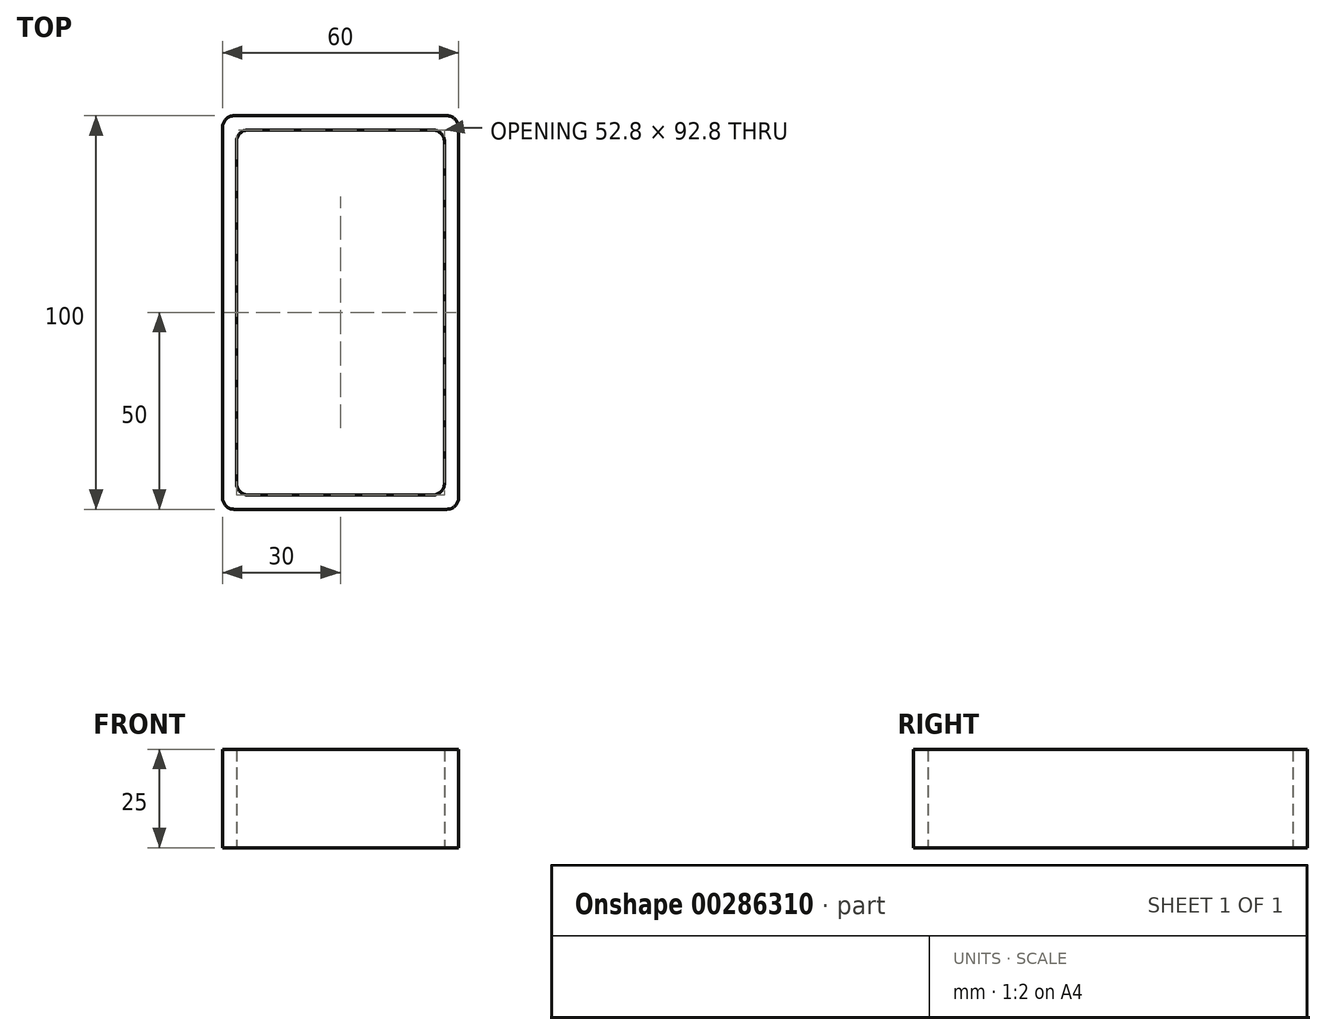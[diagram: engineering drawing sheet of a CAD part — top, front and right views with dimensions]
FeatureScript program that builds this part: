
annotation { "Feature Type Name" : "Feature", "Feature Type Description" : "" }
export const myFeature = defineFeature(function(context is Context, id is Id, definition is map)
    precondition{}
    {
        {
            var Q0;
            Q0=qCreatedBy(makeId("Top.planeOp"),FACE);
            var sketch = newSketch(context, id + "F0", { "sketchPlane" : qUnion([Q0])});
            skLineSegment(sketch, "E0", {"start": v(0, -3) * mm, "end": v(0, -97) * mm});
            skLineSegment(sketch, "E1", {"start": v(3, -100) * mm, "end": v(57, -100) * mm});
            skLineSegment(sketch, "E2", {"start": v(60, -97) * mm, "end": v(60, -3) * mm});
            skLineSegment(sketch, "E3", {"start": v(57, 0) * mm, "end": v(3, 0) * mm});
            skLineSegment(sketch, "E4", {"start": v(6.6, -3.6) * mm, "end": v(53.4, -3.6) * mm});
            skLineSegment(sketch, "E5", {"start": v(56.4, -6.6) * mm, "end": v(56.4, -93.4) * mm});
            skLineSegment(sketch, "E6", {"start": v(53.4, -96.4) * mm, "end": v(6.6, -96.4) * mm});
            skLineSegment(sketch, "E7", {"start": v(3.6, -93.4) * mm, "end": v(3.6, -6.6) * mm});
            skPoint(sketch, "E8.visualSharp", {"position": v(0, 0) * mm});
            skArc(sketch, "E8.filletArc", {"start": v(3, 0) * mm, "mid": v(0.88, -0.88) * mm, "end": v(0, -3) * mm});
            skPoint(sketch, "E9.visualSharp", {"position": v(3.6, -3.6) * mm});
            skArc(sketch, "E9.filletArc", {"start": v(6.6, -3.6) * mm, "mid": v(4.48, -4.48) * mm, "end": v(3.6, -6.6) * mm});
            skPoint(sketch, "E10.visualSharp", {"position": v(60, 0) * mm});
            skArc(sketch, "E10.filletArc", {"start": v(60, -3) * mm, "mid": v(59.12, -0.88) * mm, "end": v(57, 0) * mm});
            skPoint(sketch, "E11.visualSharp", {"position": v(56.4, -3.6) * mm});
            skArc(sketch, "E11.filletArc", {"start": v(56.4, -6.6) * mm, "mid": v(55.52, -4.48) * mm, "end": v(53.4, -3.6) * mm});
            skPoint(sketch, "E12.visualSharp", {"position": v(56.4, -96.4) * mm});
            skArc(sketch, "E12.filletArc", {"start": v(53.4, -96.4) * mm, "mid": v(55.52, -95.52) * mm, "end": v(56.4, -93.4) * mm});
            skPoint(sketch, "E13.visualSharp", {"position": v(60, -100) * mm});
            skArc(sketch, "E13.filletArc", {"start": v(57, -100) * mm, "mid": v(59.12, -99.12) * mm, "end": v(60, -97) * mm});
            skPoint(sketch, "E14.visualSharp", {"position": v(3.6, -96.4) * mm});
            skArc(sketch, "E14.filletArc", {"start": v(3.6, -93.4) * mm, "mid": v(4.48, -95.52) * mm, "end": v(6.6, -96.4) * mm});
            skPoint(sketch, "E15.visualSharp", {"position": v(0, -100) * mm});
            skArc(sketch, "E15.filletArc", {"start": v(0, -97) * mm, "mid": v(0.88, -99.12) * mm, "end": v(3, -100) * mm});
            skSolve(sketch);
        }
        {
            var Q0;
            Q0 = qSketchRegion(id + "F0", true);
            extrude(context, id + "F1", {"entities" : qUnion([Q0]), "depth" : 25 * mm});
        }
    });
